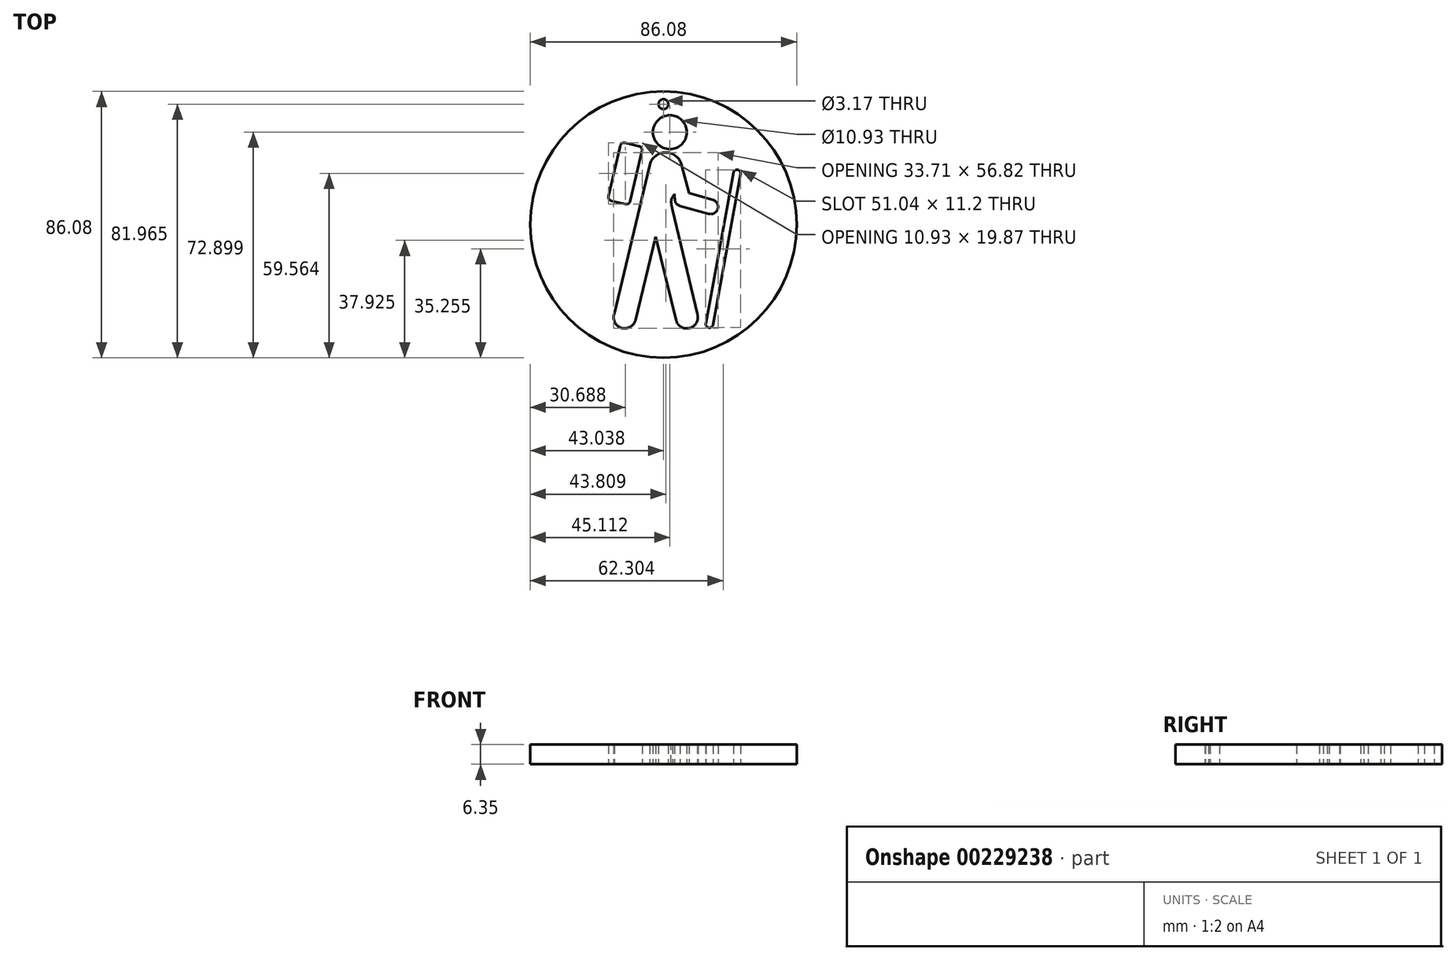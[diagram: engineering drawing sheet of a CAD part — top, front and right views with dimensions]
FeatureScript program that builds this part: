
annotation { "Feature Type Name" : "Feature", "Feature Type Description" : "" }
export const myFeature = defineFeature(function(context is Context, id is Id, definition is map)
    precondition{}
    {
        {
            var Q0;
            Q0=qCreatedBy(makeId("Top.planeOp"),FACE);
            var sketch = newSketch(context, id + "F0", { "sketchPlane" : qUnion([Q0])});
            skCircle(sketch, "E0", {"center": v(-11.87, 21.62) * mm, "radius": 5.46 * mm});
            skPoint(sketch, "E0.first.point", {"position": v(-11.95, 16.16) * mm});
            skPoint(sketch, "E0.second.point", {"position": v(-11.64, 27.08) * mm});
            skPoint(sketch, "E0.third.point", {"position": v(-6.4, 21.81) * mm});
            skLineSegment(sketch, "E1", {"start": v(-26.2, -1.62) * mm, "end": v(-30.78, -0.55) * mm});
            skLineSegment(sketch, "E2", {"start": v(-31.72, 0.98) * mm, "end": v(-27.9, 17.24) * mm});
            skLineSegment(sketch, "E3", {"start": v(-26.38, 18.19) * mm, "end": v(-21.8, 17.11) * mm});
            skLineSegment(sketch, "E4", {"start": v(-20.86, 15.59) * mm, "end": v(-24.68, -0.67) * mm});
            skArc(sketch, "E5", {"start": v(-9.9, -39.05) * mm, "mid": v(-5.38, -41.64) * mm, "end": v(-3.01, -37) * mm});
            skLineSegment(sketch, "E6", {"start": v(-23, -39.05) * mm, "end": v(-16.48, -12.11) * mm});
            skLineSegment(sketch, "E7", {"start": v(-16.48, -12.11) * mm, "end": v(-9.9, -39.05) * mm});
            skLineSegment(sketch, "E8", {"start": v(-3.01, -37) * mm, "end": v(-10.95, -3.55) * mm});
            skFitSpline(sketch, "E9", {"points": [v(-10.95, -3.55) * mm, v(-11.36, -1.9) * mm, v(-11.34, 0) * mm, v(-10.41, 1.64) * mm], "startDerivative": vector(-1.45, 4.86) * mm, "endDerivative": vector(2.8, 4.38) * mm});
            skFitSpline(sketch, "E10", {"points": [v(-10.41, 1.64) * mm, v(-10.28, 0) * mm, v(-9.96, -1.24) * mm, v(-8.56, -2.23) * mm], "startDerivative": vector(0.69, -4.63) * mm, "endDerivative": vector(5.58, -2) * mm});
            skLineSegment(sketch, "E11", {"start": v(-8.56, -2.23) * mm, "end": v(0.7, -4.77) * mm});
            skArc(sketch, "E12", {"start": v(0.7, -4.77) * mm, "mid": v(3.62, -3.1) * mm, "end": v(1.95, -0.18) * mm});
            skLineSegment(sketch, "E13", {"start": v(1.95, -0.18) * mm, "end": v(-5.7, 1.92) * mm});
            skLineSegment(sketch, "E14", {"start": v(-5.7, 1.92) * mm, "end": v(-8.03, 11.02) * mm});
            skArc(sketch, "E15", {"start": v(-8.03, 11.02) * mm, "mid": v(-13.23, 15.05) * mm, "end": v(-18.43, 11.02) * mm});
            skLineSegment(sketch, "E16", {"start": v(-29.82, -37) * mm, "end": v(-18.43, 11.02) * mm});
            skArc(sketch, "E17", {"start": v(-0.26, -40.08) * mm, "mid": v(0.65, -41.53) * mm, "end": v(2.09, -40.61) * mm});
            skLineSegment(sketch, "E18", {"start": v(2.09, -40.61) * mm, "end": v(10.93, 8.16) * mm});
            skArc(sketch, "E19", {"start": v(10.93, 8.16) * mm, "mid": v(9.99, 9.5) * mm, "end": v(8.68, 8.53) * mm});
            skLineSegment(sketch, "E20", {"start": v(8.68, 8.53) * mm, "end": v(-0.26, -40.08) * mm});
            skPoint(sketch, "E21.visualSharp", {"position": v(-27.62, 18.48) * mm});
            skArc(sketch, "E21.filletArc", {"start": v(-26.38, 18.19) * mm, "mid": v(-27.34, 18.03) * mm, "end": v(-27.9, 17.24) * mm});
            skPoint(sketch, "E22.visualSharp", {"position": v(-20.57, 16.82) * mm});
            skArc(sketch, "E22.filletArc", {"start": v(-20.86, 15.59) * mm, "mid": v(-21.02, 16.55) * mm, "end": v(-21.8, 17.11) * mm});
            skPoint(sketch, "E23.visualSharp", {"position": v(-24.97, -1.9) * mm});
            skArc(sketch, "E23.filletArc", {"start": v(-26.2, -1.62) * mm, "mid": v(-25.24, -1.46) * mm, "end": v(-24.68, -0.67) * mm});
            skPoint(sketch, "E24.visualSharp", {"position": v(-32.01, -0.26) * mm});
            skArc(sketch, "E24.filletArc", {"start": v(-31.72, 0.98) * mm, "mid": v(-31.57, 0.02) * mm, "end": v(-30.78, -0.55) * mm});
            skArc(sketch, "E25", {"start": v(-29.82, -37) * mm, "mid": v(-27.48, -41.63) * mm, "end": v(-23, -39.05) * mm});
            skSolve(sketch);
        }
        {
            var Q0;
            Q0=qCreatedBy(makeId("Top.planeOp"),FACE);
            var sketch = newSketch(context, id + "F1", { "sketchPlane" : qUnion([Q0])});
            skCircle(sketch, "E26", {"center": v(-13.94, -8.24) * mm, "radius": 43.04 * mm});
            skCircle(sketch, "E27", {"center": v(-13.94, 30.69) * mm, "radius": 1.59 * mm});
            skSolve(sketch);
        }
        {
            var Q0;
            Q0=makeQuery(id+"F1.imprint","IMPRINT",FACE,{"disambiguationData":[TD([[makeQuery(id+"F1.imprint","IMPRINT",EDGE,{"derivedFrom":sQuery(id+"F1.wireOp",EDGE,"E26")}),1.0]])]});
            extrude(context, id + "F2", {"entities" : qUnion([Q0]), "depth" : 6.35 * mm});
        }
        {
            var Q0;
            Q0 = qSketchRegion(id + "F0", true);
            extrude(context, id + "F3", {"entities" : qUnion([Q0]), "operationType" : NewBodyOperationType.REMOVE, "depth" : 6.35 * mm});
        }
    });
